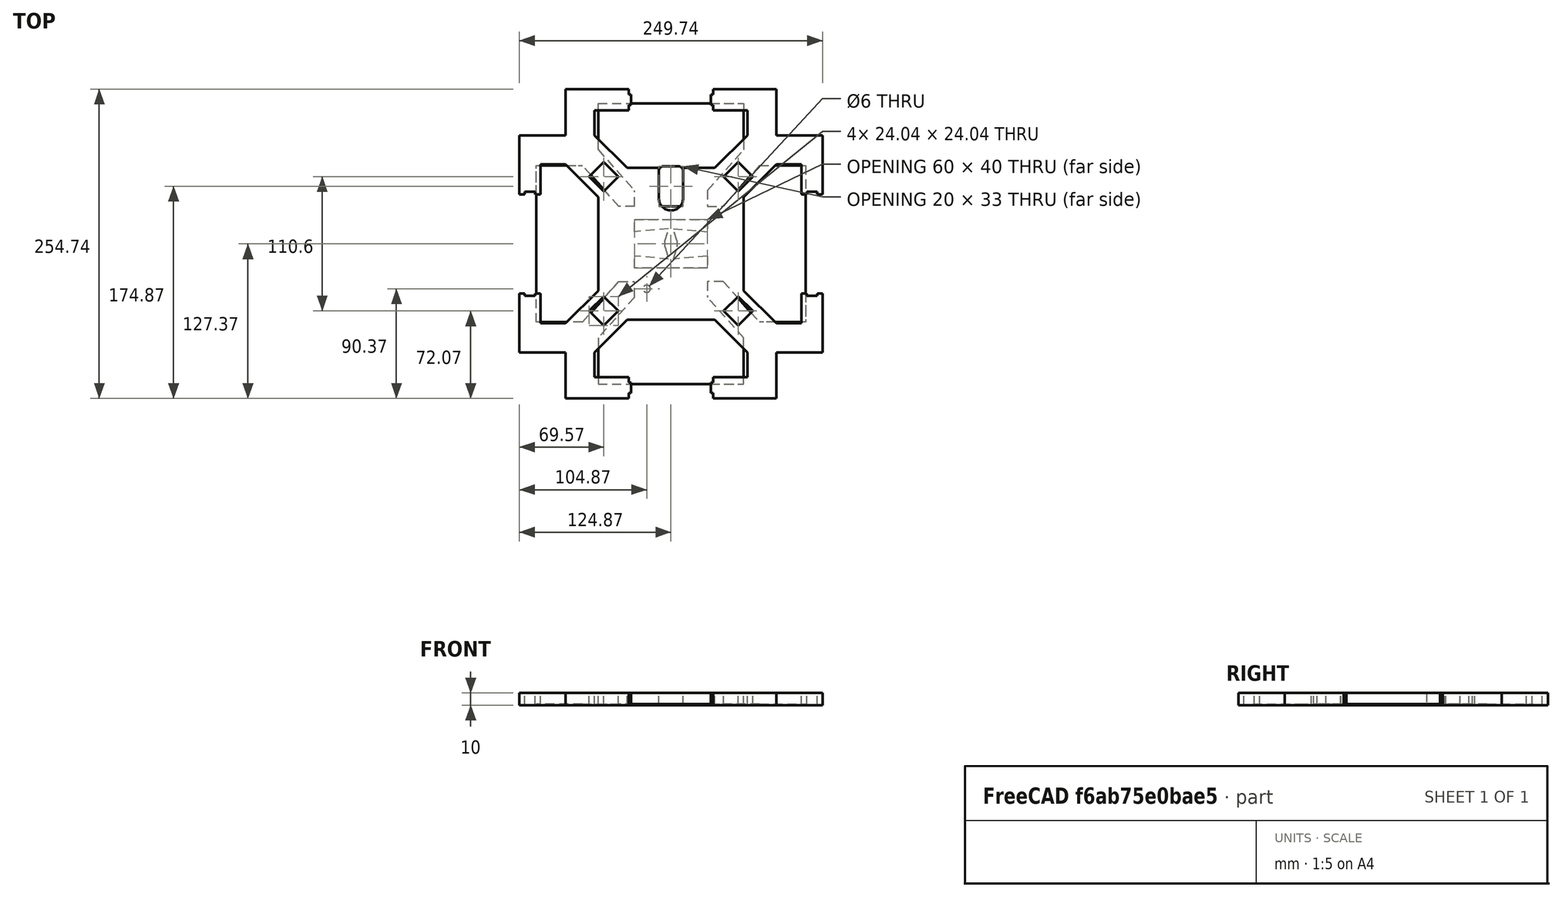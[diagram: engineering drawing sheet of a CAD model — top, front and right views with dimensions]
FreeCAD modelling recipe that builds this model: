
FCSTD DOCUMENT  (FreeCAD 0.20R29410 (Git))
Label: cardboard_insert
License: All rights reserved
LicenseURL: http://en.wikipedia.org/wiki/All_rights_reserved
objects: Sketcher::SketchObject×2, PartDesign::Pad×2, PartDesign::Body×2, TechDraw::DrawSVGTemplate×2, TechDraw::DrawProjGroupItem×2, TechDraw::DrawProjGroup×2, TechDraw::DrawViewDimension×2, TechDraw::DrawPage×2
note: 8 computed .brp shape members not serialized (recipe doc carries the construction recipe); baked Part::Feature solids carry a one-line shape summary decoded from their .brp

FEATURE [Sketcher::SketchObject] Sketch
  FullyConstrained = true
  MapMode = 5
  Support = -> [XY_Plane]
  expr: Constraints[378] = 6.65 + 1
  expr: Constraints[453] = 10.18 + 1
  sketch-geometry (214):
    g0: LineSegment StartX=53.3 StartY=53.3 StartZ=0 EndX=-53.3 EndY=53.3 EndZ=0
    g1: LineSegment StartX=-53.3 StartY=53.3 StartZ=0 EndX=-53.3 EndY=-53.3 EndZ=0
    g2: LineSegment StartX=-53.3 StartY=-53.3 StartZ=0 EndX=53.3 EndY=-53.3 EndZ=0
    g3: LineSegment StartX=53.3 StartY=-53.3 StartZ=0 EndX=53.3 EndY=53.3 EndZ=0
    g4: Circle CenterX=0 CenterY=0 CenterZ=0 NormalX=0 NormalY=0 NormalZ=1 AngleXU=0 Radius=75.3776
    g5: LineSegment StartX=-36.0792 StartY=62.5 StartZ=0 EndX=36.0792 EndY=62.5 EndZ=0
    g6: LineSegment StartX=-36.0792 StartY=-62.5 StartZ=0 EndX=36.0792 EndY=-62.5 EndZ=0
    g7: LineSegment StartX=-60 StartY=-38.5792 StartZ=0 EndX=-60 EndY=38.5792 EndZ=0
    g8: LineSegment StartX=60 StartY=38.5792 StartZ=0 EndX=60 EndY=-38.5792 EndZ=0
    g9: LineSegment StartX=36.0792 StartY=-62.5 StartZ=0 EndX=62.9492 EndY=-89.3701 EndZ=0
    g10: LineSegment StartX=60 StartY=-38.5792 StartZ=0 EndX=86.8701 EndY=-65.4492 EndZ=0
    g11: LineSegment StartX=60 StartY=38.5792 StartZ=0 EndX=86.8701 EndY=65.4492 EndZ=0
    g12: LineSegment StartX=36.0792 StartY=62.5 StartZ=0 EndX=62.9492 EndY=89.3701 EndZ=0
    g13: LineSegment StartX=62.9492 StartY=89.3701 StartZ=0 EndX=86.8701 EndY=65.4492 EndZ=0
    g14: LineSegment StartX=86.8701 StartY=-65.4492 StartZ=0 EndX=62.9492 EndY=-89.3701 EndZ=0
    g15: LineSegment StartX=-36.0792 StartY=-62.5 StartZ=0 EndX=-62.9492 EndY=-89.3701 EndZ=0
    g16: LineSegment StartX=-60 StartY=-38.5792 StartZ=0 EndX=-86.8701 EndY=-65.4492 EndZ=0
    g17: LineSegment StartX=-86.8701 StartY=-65.4492 StartZ=0 EndX=-62.9492 EndY=-89.3701 EndZ=0
    g18: LineSegment StartX=-60 StartY=38.5792 StartZ=0 EndX=-86.8701 EndY=65.4492 EndZ=0
    g19: LineSegment StartX=-86.8701 StartY=65.4492 StartZ=0 EndX=-62.9492 EndY=89.3701 EndZ=0
    g20: LineSegment StartX=-62.9492 StartY=89.3701 StartZ=0 EndX=-36.0792 EndY=62.5 EndZ=0
    g21: LineSegment StartX=-60 StartY=38.5792 StartZ=0 EndX=-7.1e-15 EndY=0 EndZ=0
    g22: LineSegment StartX=-7.1e-15 StartY=0 StartZ=0 EndX=60 EndY=-38.5792 EndZ=0
    g23: LineSegment StartX=60 StartY=38.5792 StartZ=0 EndX=0 EndY=0 EndZ=0
    g24: LineSegment StartX=0 StartY=0 StartZ=0 EndX=-60 EndY=-38.5792 EndZ=0
    g25: LineSegment StartX=0 StartY=0 StartZ=0 EndX=-36.0792 EndY=62.5 EndZ=0
    g26: LineSegment StartX=36.0792 StartY=62.5 StartZ=0 EndX=0 EndY=0 EndZ=0
    g27: LineSegment StartX=0 StartY=0 StartZ=0 EndX=-36.0792 EndY=-62.5 EndZ=0
    g28: LineSegment StartX=36.0792 StartY=-62.5 StartZ=0 EndX=0 EndY=0 EndZ=0
    g29: LineSegment StartX=-60 StartY=38.5792 StartZ=0 EndX=-36.0792 EndY=62.5 EndZ=0
    g30: LineSegment StartX=36.0792 StartY=62.5 StartZ=0 EndX=60 EndY=38.5792 EndZ=0
    g31: LineSegment StartX=60 StartY=-38.5792 StartZ=0 EndX=36.0792 EndY=-62.5 EndZ=0
    g32: LineSegment StartX=-36.0792 StartY=-62.5 StartZ=0 EndX=-60 EndY=-38.5792 EndZ=0
    g33: LineSegment StartX=-86.8701 StartY=65.4492 StartZ=0 EndX=-86.8701 EndY=89.3701 EndZ=0
    g34: LineSegment StartX=-86.8701 StartY=89.3701 StartZ=0 EndX=-62.9492 EndY=89.3701 EndZ=0
    g35: LineSegment StartX=62.9492 StartY=89.3701 StartZ=0 EndX=86.8701 EndY=89.3701 EndZ=0
    g36: LineSegment StartX=86.8701 StartY=89.3701 StartZ=0 EndX=86.8701 EndY=65.4492 EndZ=0
    g37: LineSegment StartX=62.9492 StartY=-89.3701 StartZ=0 EndX=86.8701 EndY=-89.3701 EndZ=0
    g38: LineSegment StartX=86.8701 StartY=-65.4492 StartZ=0 EndX=86.8701 EndY=-89.3701 EndZ=0
    g39: LineSegment StartX=-86.8701 StartY=-65.4492 StartZ=0 EndX=-86.8701 EndY=-89.3701 EndZ=0
    g40: LineSegment StartX=-62.9492 StartY=-89.3701 StartZ=0 EndX=-86.8701 EndY=-89.3701 EndZ=0
    g41: LineSegment StartX=-86.8701 StartY=65.4492 StartZ=0 EndX=-124.87 EndY=65.4492 EndZ=0
    g42: LineSegment StartX=-124.87 StartY=65.4492 StartZ=0 EndX=-124.87 EndY=89.3701 EndZ=0
    g43: LineSegment StartX=-124.87 StartY=89.3701 StartZ=0 EndX=-86.8701 EndY=89.3701 EndZ=0
    g44: LineSegment StartX=-86.8701 StartY=89.3701 StartZ=0 EndX=-86.8701 EndY=127.37 EndZ=0
    g45: LineSegment StartX=-86.8701 StartY=127.37 StartZ=0 EndX=-62.9492 EndY=127.37 EndZ=0
    g46: LineSegment StartX=-62.9492 StartY=127.37 StartZ=0 EndX=-62.9492 EndY=89.3701 EndZ=0
    g47: LineSegment StartX=-86.8701 StartY=-65.4492 StartZ=0 EndX=-124.87 EndY=-65.4492 EndZ=0
    g48: LineSegment StartX=-124.87 StartY=-65.4492 StartZ=0 EndX=-124.87 EndY=-89.3701 EndZ=0
    g49: LineSegment StartX=-124.87 StartY=-89.3701 StartZ=0 EndX=-86.8701 EndY=-89.3701 EndZ=0
    g50: LineSegment StartX=-86.8701 StartY=-89.3701 StartZ=0 EndX=-86.8701 EndY=-127.37 EndZ=0
    g51: LineSegment StartX=-86.8701 StartY=-127.37 StartZ=0 EndX=-62.9492 EndY=-127.37 EndZ=0
    g52: LineSegment StartX=-62.9492 StartY=-127.37 StartZ=0 EndX=-62.9492 EndY=-89.3701 EndZ=0
    g53: LineSegment StartX=62.9492 StartY=-89.3701 StartZ=0 EndX=62.9492 EndY=-127.37 EndZ=0
    g54: LineSegment StartX=62.9492 StartY=-127.37 StartZ=0 EndX=86.8701 EndY=-127.37 EndZ=0
    g55: LineSegment StartX=86.8701 StartY=-127.37 StartZ=0 EndX=86.8701 EndY=-89.3701 EndZ=0
    g56: LineSegment StartX=86.8701 StartY=-89.3701 StartZ=0 EndX=124.87 EndY=-89.3701 EndZ=0
    g57: LineSegment StartX=124.87 StartY=-89.3701 StartZ=0 EndX=124.87 EndY=-65.4492 EndZ=0
    g58: LineSegment StartX=124.87 StartY=-65.4492 StartZ=0 EndX=86.8701 EndY=-65.4492 EndZ=0
    g59: LineSegment StartX=86.8701 StartY=65.4492 StartZ=0 EndX=124.87 EndY=65.4492 EndZ=0
    g60: LineSegment StartX=124.87 StartY=65.4492 StartZ=0 EndX=124.87 EndY=89.3701 EndZ=0
    g61: LineSegment StartX=124.87 StartY=89.3701 StartZ=0 EndX=86.8701 EndY=89.3701 EndZ=0
    g62: LineSegment StartX=86.8701 StartY=89.3701 StartZ=0 EndX=86.8701 EndY=127.37 EndZ=0
    g63: LineSegment StartX=86.8701 StartY=127.37 StartZ=0 EndX=62.9492 EndY=127.37 EndZ=0
    g64: LineSegment StartX=62.9492 StartY=127.37 StartZ=0 EndX=62.9492 EndY=89.3701 EndZ=0
    g65: LineSegment StartX=-55.3 StartY=43.2792 StartZ=0 EndX=-67.3208 EndY=55.3 EndZ=0
    g66: LineSegment StartX=-67.3208 StartY=55.3 StartZ=0 EndX=-55.3 EndY=67.3208 EndZ=0
    g67: LineSegment StartX=-55.3 StartY=67.3208 StartZ=0 EndX=-43.2792 EndY=55.3 EndZ=0
    g68: LineSegment StartX=-43.2792 StartY=55.3 StartZ=0 EndX=-55.3 EndY=43.2792 EndZ=0
    g69: LineSegment StartX=43.2792 StartY=55.3 StartZ=0 EndX=55.3 EndY=67.3208 EndZ=0
    g70: LineSegment StartX=55.3 StartY=67.3208 StartZ=0 EndX=67.3208 EndY=55.3 EndZ=0
    g71: LineSegment StartX=67.3208 StartY=55.3 StartZ=0 EndX=55.3 EndY=43.2792 EndZ=0
    g72: LineSegment StartX=55.3 StartY=43.2792 StartZ=0 EndX=43.2792 EndY=55.3 EndZ=0
    g73: LineSegment StartX=43.2792 StartY=-55.3 StartZ=0 EndX=55.3 EndY=-67.3208 EndZ=0
    g74: LineSegment StartX=55.3 StartY=-67.3208 StartZ=0 EndX=67.3208 EndY=-55.3 EndZ=0
    g75: LineSegment StartX=67.3208 StartY=-55.3 StartZ=0 EndX=55.3 EndY=-43.2792 EndZ=0
    g76: LineSegment StartX=55.3 StartY=-43.2792 StartZ=0 EndX=43.2792 EndY=-55.3 EndZ=0
    g77: LineSegment StartX=-43.2792 StartY=-55.3 StartZ=0 EndX=-55.3 EndY=-67.3208 EndZ=0
    g78: LineSegment StartX=-55.3 StartY=-67.3208 StartZ=0 EndX=-67.3208 EndY=-55.3 EndZ=0
    g79: LineSegment StartX=-67.3208 StartY=-55.3 StartZ=0 EndX=-55.3 EndY=-43.2792 EndZ=0
    g80: LineSegment StartX=-55.3 StartY=-43.2792 StartZ=0 EndX=-43.2792 EndY=-55.3 EndZ=0
    g81: LineSegment StartX=-55.3 StartY=43.2792 StartZ=0 EndX=0 EndY=0 EndZ=0
    g82: LineSegment StartX=0 StartY=0 StartZ=0 EndX=-43.2792 EndY=55.3 EndZ=0
    g83: LineSegment StartX=43.2792 StartY=55.3 StartZ=0 EndX=0 EndY=0 EndZ=0
    g84: LineSegment StartX=0 StartY=0 StartZ=0 EndX=55.3 EndY=43.2792 EndZ=0
    g85: LineSegment StartX=55.3 StartY=-43.2792 StartZ=0 EndX=0 EndY=7.1e-15 EndZ=0
    g86: LineSegment StartX=0 StartY=0 StartZ=0 EndX=43.2792 EndY=-55.3 EndZ=0
    g87: LineSegment StartX=-43.2792 StartY=-55.3 StartZ=0 EndX=0 EndY=0 EndZ=0
    g88: LineSegment StartX=0 StartY=0 StartZ=0 EndX=-55.3 EndY=-43.2792 EndZ=0
    g89: LineSegment StartX=-124.87 StartY=65.4492 StartZ=0 EndX=-124.87 EndY=62.4492 EndZ=0
    g90: LineSegment StartX=-124.87 StartY=62.4492 StartZ=0 EndX=-107.37 EndY=62.4492 EndZ=0
    g91: LineSegment StartX=-107.37 StartY=62.4492 StartZ=0 EndX=-107.37 EndY=65.4492 EndZ=0
    g92: LineSegment StartX=-107.37 StartY=65.4492 StartZ=0 EndX=-86.8701 EndY=65.4492 EndZ=0
    g93: LineSegment StartX=-62.9492 StartY=89.3701 StartZ=0 EndX=-62.9492 EndY=109.87 EndZ=0
    g94: LineSegment StartX=-62.9492 StartY=109.87 StartZ=0 EndX=-59.9492 EndY=109.87 EndZ=0
    g95: LineSegment StartX=-59.9492 StartY=109.87 StartZ=0 EndX=-59.9492 EndY=127.37 EndZ=0
    g96: LineSegment StartX=-59.9492 StartY=127.37 StartZ=0 EndX=-62.9492 EndY=127.37 EndZ=0
    g97: LineSegment StartX=62.9492 StartY=127.37 StartZ=0 EndX=59.9492 EndY=127.37 EndZ=0
    g98: LineSegment StartX=59.9492 StartY=127.37 StartZ=0 EndX=59.9492 EndY=109.87 EndZ=0
    g99: LineSegment StartX=59.9492 StartY=109.87 StartZ=0 EndX=62.9492 EndY=109.87 EndZ=0
    g100: LineSegment StartX=62.9492 StartY=109.87 StartZ=0 EndX=62.9492 EndY=89.3701 EndZ=0
    g101: LineSegment StartX=86.8701 StartY=65.4492 StartZ=0 EndX=107.37 EndY=65.4492 EndZ=0
    g102: LineSegment StartX=107.37 StartY=65.4492 StartZ=0 EndX=107.37 EndY=62.4492 EndZ=0
    g103: LineSegment StartX=107.37 StartY=62.4492 StartZ=0 EndX=124.87 EndY=62.4492 EndZ=0
    g104: LineSegment StartX=124.87 StartY=62.4492 StartZ=0 EndX=124.87 EndY=65.4492 EndZ=0
    g105: LineSegment StartX=86.8701 StartY=-65.4492 StartZ=0 EndX=107.37 EndY=-65.4492 EndZ=0
    g106: LineSegment StartX=107.37 StartY=-65.4492 StartZ=0 EndX=107.37 EndY=-62.4492 EndZ=0
    g107: LineSegment StartX=107.37 StartY=-62.4492 StartZ=0 EndX=124.87 EndY=-62.4492 EndZ=0
    g108: LineSegment StartX=124.87 StartY=-62.4492 StartZ=0 EndX=124.87 EndY=-65.4492 EndZ=0
    g109: LineSegment StartX=62.9492 StartY=-89.3701 StartZ=0 EndX=62.9492 EndY=-109.87 EndZ=0
    g110: LineSegment StartX=62.9492 StartY=-109.87 StartZ=0 EndX=59.9492 EndY=-109.87 EndZ=0
    g111: LineSegment StartX=59.9492 StartY=-109.87 StartZ=0 EndX=59.9492 EndY=-127.37 EndZ=0
    g112: LineSegment StartX=59.9492 StartY=-127.37 StartZ=0 EndX=62.9492 EndY=-127.37 EndZ=0
    g113: LineSegment StartX=-62.9492 StartY=-127.37 StartZ=0 EndX=-59.9492 EndY=-127.37 EndZ=0
    g114: LineSegment StartX=-59.9492 StartY=-127.37 StartZ=0 EndX=-59.9492 EndY=-109.87 EndZ=0
    g115: LineSegment StartX=-59.9492 StartY=-109.87 StartZ=0 EndX=-62.9492 EndY=-109.87 EndZ=0
    g116: LineSegment StartX=-62.9492 StartY=-109.87 StartZ=0 EndX=-62.9492 EndY=-89.3701 EndZ=0
    g117: LineSegment StartX=-124.87 StartY=-65.4492 StartZ=0 EndX=-124.87 EndY=-62.4492 EndZ=0
    g118: LineSegment StartX=-124.87 StartY=-62.4492 StartZ=0 EndX=-107.37 EndY=-62.4492 EndZ=0
    g119: LineSegment StartX=-107.37 StartY=-62.4492 StartZ=0 EndX=-107.37 EndY=-65.4492 EndZ=0
    g120: LineSegment StartX=-107.37 StartY=-65.4492 StartZ=0 EndX=-86.8701 EndY=-65.4492 EndZ=0
    g121: LineSegment StartX=-124.87 StartY=62.4492 StartZ=0 EndX=-124.87 EndY=54.7992 EndZ=0
    g122: LineSegment StartX=-124.87 StartY=54.7992 StartZ=0 EndX=-107.37 EndY=54.7992 EndZ=0
    g123: LineSegment StartX=-107.37 StartY=54.7992 StartZ=0 EndX=-107.37 EndY=62.4492 EndZ=0
    g124: LineSegment StartX=-59.9492 StartY=127.37 StartZ=0 EndX=-48.7692 EndY=127.37 EndZ=0
    g125: LineSegment StartX=-48.7692 StartY=127.37 StartZ=0 EndX=-48.7692 EndY=109.87 EndZ=0
    g126: LineSegment StartX=-48.7692 StartY=109.87 StartZ=0 EndX=-59.9492 EndY=109.87 EndZ=0
    g127: LineSegment StartX=59.9492 StartY=127.37 StartZ=0 EndX=48.7692 EndY=127.37 EndZ=0
    g128: LineSegment StartX=48.7692 StartY=127.37 StartZ=0 EndX=48.7692 EndY=109.87 EndZ=0
    g129: LineSegment StartX=48.7692 StartY=109.87 StartZ=0 EndX=59.9492 EndY=109.87 EndZ=0
    g130: LineSegment StartX=107.37 StartY=62.4492 StartZ=0 EndX=107.37 EndY=54.7992 EndZ=0
    g131: LineSegment StartX=107.37 StartY=54.7992 StartZ=0 EndX=124.87 EndY=54.7992 EndZ=0
    g132: LineSegment StartX=124.87 StartY=54.7992 StartZ=0 EndX=124.87 EndY=62.4492 EndZ=0
    g133: LineSegment StartX=107.37 StartY=-62.4492 StartZ=0 EndX=107.37 EndY=-54.7992 EndZ=0
    g134: LineSegment StartX=107.37 StartY=-54.7992 StartZ=0 EndX=124.87 EndY=-54.7992 EndZ=0
    g135: LineSegment StartX=124.87 StartY=-54.7992 StartZ=0 EndX=124.87 EndY=-62.4492 EndZ=0
    g136: LineSegment StartX=59.9492 StartY=-109.87 StartZ=0 EndX=48.7692 EndY=-109.87 EndZ=0
    g137: LineSegment StartX=48.7692 StartY=-109.87 StartZ=0 EndX=48.7692 EndY=-127.37 EndZ=0
    g138: LineSegment StartX=48.7692 StartY=-127.37 StartZ=0 EndX=59.9492 EndY=-127.37 EndZ=0
    g139: LineSegment StartX=-59.9492 StartY=-127.37 StartZ=0 EndX=-48.7692 EndY=-127.37 EndZ=0
    g140: LineSegment StartX=-48.7692 StartY=-127.37 StartZ=0 EndX=-48.7692 EndY=-109.87 EndZ=0
    g141: LineSegment StartX=-48.7692 StartY=-109.87 StartZ=0 EndX=-59.9492 EndY=-109.87 EndZ=0
    g142: LineSegment StartX=-124.87 StartY=-62.4492 StartZ=0 EndX=-124.87 EndY=-54.7992 EndZ=0
    g143: LineSegment StartX=-124.87 StartY=-54.7992 StartZ=0 EndX=-107.37 EndY=-54.7992 EndZ=0
    g144: LineSegment StartX=-107.37 StartY=-54.7992 StartZ=0 EndX=-107.37 EndY=-62.4492 EndZ=0
    g145: LineSegment StartX=-36.0792 StartY=62.5 StartZ=0 EndX=-10 EndY=62.5 EndZ=0
    g146: LineSegment StartX=36.0792 StartY=62.5 StartZ=0 EndX=10 EndY=62.5 EndZ=0
    g147: LineSegment StartX=-10 StartY=62.5 StartZ=0 EndX=-10 EndY=37.5 EndZ=0
    g148: LineSegment StartX=10 StartY=62.5 StartZ=0 EndX=10 EndY=37.5 EndZ=0
    g149: ArcOfCircle CenterX=0 CenterY=37.5 CenterZ=0 NormalX=0 NormalY=0 NormalZ=1 AngleXU=0 Radius=10 StartAngle=3.14159 EndAngle=6.28319
    g150: LineSegment StartX=-124.87 StartY=54.7992 StartZ=0 EndX=-124.87 EndY=40.7992 EndZ=0
    g151: LineSegment StartX=-124.87 StartY=40.7992 StartZ=0 EndX=-107.37 EndY=40.7992 EndZ=0
    g152: LineSegment StartX=-107.37 StartY=40.7992 StartZ=0 EndX=-107.37 EndY=54.7992 EndZ=0
    g153: LineSegment StartX=-48.7692 StartY=127.37 StartZ=0 EndX=-34.7692 EndY=127.37 EndZ=0
    g154: LineSegment StartX=-34.7692 StartY=127.37 StartZ=0 EndX=-34.7692 EndY=109.87 EndZ=0
    g155: LineSegment StartX=-34.7692 StartY=109.87 StartZ=0 EndX=-48.7692 EndY=109.87 EndZ=0
    g156: LineSegment StartX=48.7692 StartY=127.37 StartZ=0 EndX=34.7692 EndY=127.37 EndZ=0
    g157: LineSegment StartX=34.7692 StartY=127.37 StartZ=0 EndX=34.7692 EndY=109.87 EndZ=0
    g158: LineSegment StartX=34.7692 StartY=109.87 StartZ=0 EndX=48.7692 EndY=109.87 EndZ=0
    g159: LineSegment StartX=107.37 StartY=54.7992 StartZ=0 EndX=107.37 EndY=40.7992 EndZ=0
    g160: LineSegment StartX=107.37 StartY=40.7992 StartZ=0 EndX=124.87 EndY=40.7992 EndZ=0
    g161: LineSegment StartX=124.87 StartY=40.7992 StartZ=0 EndX=124.87 EndY=54.7992 EndZ=0
    g162: LineSegment StartX=124.87 StartY=-54.7992 StartZ=0 EndX=124.87 EndY=-40.7992 EndZ=0
    g163: LineSegment StartX=124.87 StartY=-40.7992 StartZ=0 EndX=107.37 EndY=-40.7992 EndZ=0
    g164: LineSegment StartX=107.37 StartY=-40.7992 StartZ=0 EndX=107.37 EndY=-54.7992 EndZ=0
    g165: LineSegment StartX=48.7692 StartY=-109.87 StartZ=0 EndX=34.7692 EndY=-109.87 EndZ=0
    g166: LineSegment StartX=34.7692 StartY=-109.87 StartZ=0 EndX=34.7692 EndY=-127.37 EndZ=0
    g167: LineSegment StartX=34.7692 StartY=-127.37 StartZ=0 EndX=48.7692 EndY=-127.37 EndZ=0
    g168: LineSegment StartX=-48.7692 StartY=-109.87 StartZ=0 EndX=-34.7692 EndY=-109.87 EndZ=0
    g169: LineSegment StartX=-34.7692 StartY=-109.87 StartZ=0 EndX=-34.7692 EndY=-127.37 EndZ=0
    g170: LineSegment StartX=-34.7692 StartY=-127.37 StartZ=0 EndX=-48.7692 EndY=-127.37 EndZ=0
    g171: LineSegment StartX=-124.87 StartY=-54.7992 StartZ=0 EndX=-124.87 EndY=-40.7992 EndZ=0
    g172: LineSegment StartX=-124.87 StartY=-40.7992 StartZ=0 EndX=-107.37 EndY=-40.7992 EndZ=0
    g173: LineSegment StartX=-107.37 StartY=-40.7992 StartZ=0 EndX=-107.37 EndY=-54.7992 EndZ=0
    g174: LineSegment StartX=-124.87 StartY=40.7992 StartZ=0 EndX=-120.37 EndY=40.7992 EndZ=0
    g175: LineSegment StartX=-120.37 StartY=40.7992 StartZ=0 EndX=-120.37 EndY=42.7992 EndZ=0
    g176: LineSegment StartX=-120.37 StartY=42.7992 StartZ=0 EndX=-111.87 EndY=42.7992 EndZ=0
    g177: LineSegment StartX=-111.87 StartY=42.7992 StartZ=0 EndX=-111.87 EndY=40.7992 EndZ=0
    g178: LineSegment StartX=-111.87 StartY=40.7992 StartZ=0 EndX=-107.37 EndY=40.7992 EndZ=0
    g179: LineSegment StartX=107.37 StartY=40.7992 StartZ=0 EndX=111.87 EndY=40.7992 EndZ=0
    g180: LineSegment StartX=111.87 StartY=40.7992 StartZ=0 EndX=111.87 EndY=42.7992 EndZ=0
    g181: LineSegment StartX=111.87 StartY=42.7992 StartZ=0 EndX=120.37 EndY=42.7992 EndZ=0
    g182: LineSegment StartX=120.37 StartY=42.7992 StartZ=0 EndX=120.37 EndY=40.7992 EndZ=0
    g183: LineSegment StartX=120.37 StartY=40.7992 StartZ=0 EndX=124.87 EndY=40.7992 EndZ=0
    g184: LineSegment StartX=107.37 StartY=-40.7992 StartZ=0 EndX=111.87 EndY=-40.7992 EndZ=0
    g185: LineSegment StartX=111.87 StartY=-40.7992 StartZ=0 EndX=111.87 EndY=-42.7992 EndZ=0
    g186: LineSegment StartX=111.87 StartY=-42.7992 StartZ=0 EndX=120.37 EndY=-42.7992 EndZ=0
    g187: LineSegment StartX=120.37 StartY=-42.7992 StartZ=0 EndX=120.37 EndY=-40.7992 EndZ=0
    g188: LineSegment StartX=120.37 StartY=-40.7992 StartZ=0 EndX=124.87 EndY=-40.7992 EndZ=0
    g189: LineSegment StartX=-124.87 StartY=-40.7992 StartZ=0 EndX=-120.37 EndY=-40.7992 EndZ=0
    g190: LineSegment StartX=-120.37 StartY=-40.7992 StartZ=0 EndX=-120.37 EndY=-42.7992 EndZ=0
    g191: LineSegment StartX=-120.37 StartY=-42.7992 StartZ=0 EndX=-111.87 EndY=-42.7992 EndZ=0
    g192: LineSegment StartX=-111.87 StartY=-42.7992 StartZ=0 EndX=-111.87 EndY=-40.7992 EndZ=0
    g193: LineSegment StartX=-111.87 StartY=-40.7992 StartZ=0 EndX=-107.37 EndY=-40.7992 EndZ=0
    g194: LineSegment StartX=-34.7692 StartY=127.37 StartZ=0 EndX=-34.7692 EndY=122.87 EndZ=0
    g195: LineSegment StartX=-34.7692 StartY=122.87 StartZ=0 EndX=-32.7692 EndY=122.87 EndZ=0
    g196: LineSegment StartX=-32.7692 StartY=122.87 StartZ=0 EndX=-32.7692 EndY=114.37 EndZ=0
    g197: LineSegment StartX=-32.7692 StartY=114.37 StartZ=0 EndX=-34.7692 EndY=114.37 EndZ=0
    g198: LineSegment StartX=-34.7692 StartY=114.37 StartZ=0 EndX=-34.7692 EndY=109.87 EndZ=0
    g199: LineSegment StartX=34.7692 StartY=127.37 StartZ=0 EndX=34.7692 EndY=122.87 EndZ=0
    g200: LineSegment StartX=34.7692 StartY=122.87 StartZ=0 EndX=32.7692 EndY=122.87 EndZ=0
    g201: LineSegment StartX=32.7692 StartY=122.87 StartZ=0 EndX=32.7692 EndY=114.37 EndZ=0
    g202: LineSegment StartX=32.7692 StartY=114.37 StartZ=0 EndX=34.7692 EndY=114.37 EndZ=0
    g203: LineSegment StartX=34.7692 StartY=114.37 StartZ=0 EndX=34.7692 EndY=109.87 EndZ=0
    g204: LineSegment StartX=-34.7692 StartY=-109.87 StartZ=0 EndX=-34.7692 EndY=-114.37 EndZ=0
    g205: LineSegment StartX=-34.7692 StartY=-114.37 StartZ=0 EndX=-32.7692 EndY=-114.37 EndZ=0
    g206: LineSegment StartX=-32.7692 StartY=-114.37 StartZ=0 EndX=-32.7692 EndY=-122.87 EndZ=0
    g207: LineSegment StartX=-32.7692 StartY=-122.87 StartZ=0 EndX=-34.7692 EndY=-122.87 EndZ=0
    g208: LineSegment StartX=-34.7692 StartY=-122.87 StartZ=0 EndX=-34.7692 EndY=-127.37 EndZ=0
    g209: LineSegment StartX=34.7692 StartY=-109.87 StartZ=0 EndX=34.7692 EndY=-114.37 EndZ=0
    g210: LineSegment StartX=34.7692 StartY=-114.37 StartZ=0 EndX=32.7692 EndY=-114.37 EndZ=0
    g211: LineSegment StartX=32.7692 StartY=-114.37 StartZ=0 EndX=32.7692 EndY=-122.87 EndZ=0
    g212: LineSegment StartX=32.7692 StartY=-122.87 StartZ=0 EndX=34.7692 EndY=-122.87 EndZ=0
    g213: LineSegment StartX=34.7692 StartY=-122.87 StartZ=0 EndX=34.7692 EndY=-127.37 EndZ=0
  constraints (575):
    c: Coincident(g0,g1)
    c: Coincident(g1,g2)
    c: Coincident(g2,g3)
    c: Coincident(g3,g0)
    c: Equal(g0,g1)
    c: Equal(g0,g2)
    c: Equal(g0,g3)
    c: PointOnObject(g0,g4)
    c: PointOnObject(g1,g4)
    c: PointOnObject(g2,g4)
    c: PointOnObject(g3,g4)
    c: Coincident(g4,g-1)
    c: Horizontal(g0)
    c: DistanceX(g0,g0) = 106.6
    c: Horizontal(g5)
    c: Horizontal(g6)
    c: Vertical(g7)
    c: Vertical(g8)
    c: Coincident(g9,g6)
    c: Coincident(g10,g8)
    c: Coincident(g11,g8)
    c: Coincident(g12,g5)
    c: Coincident(g13,g12)
    c: Coincident(g13,g11)
    c: Coincident(g14,g10)
    c: Coincident(g14,g9)
    c: Coincident(g15,g6)
    c: Coincident(g7,g16)
    c: Coincident(g16,g17)
    c: Coincident(g17,g15)
    c: Coincident(g7,g18)
    c: Coincident(g18,g19)
    c: Coincident(g19,g20)
    c: Coincident(g20,g5)
    c: Perpendicular(g19,g18)
    c: Perpendicular(g20,g19)
    c: Perpendicular(g13,g12)
    c: Perpendicular(g11,g13)
    c: Perpendicular(g14,g10)
    c: Perpendicular(g9,g14)
    c: Perpendicular(g17,g15)
    c: Perpendicular(g16,g17)
    c: Parallel(g16,g19)
    c: Parallel(g19,g12)
    c: Parallel(g12,g14)
    c: Angle(g5,g20) = 2.35619
    c: Coincident(g7,g21)
    c: Coincident(g21,g-1)
    c: Coincident(g21,g22)
    c: Coincident(g22,g8)
    c: Coincident(g8,g23)
    c: Coincident(g23,g-1)
    c: Coincident(g23,g24)
    c: Coincident(g24,g7)
    c: Coincident(g-1,g25)
    c: Coincident(g25,g5)
    c: Coincident(g5,g26)
    c: Coincident(g26,g-1)
    c: Coincident(g26,g27)
    c: Coincident(g27,g6)
    c: Coincident(g6,g28)
    c: Coincident(g28,g-1)
    c: Equal(g27,g28)
    c: Equal(g28,g26)
    c: Equal(g26,g25)
    c: Equal(g21,g24)
    c: Equal(g24,g22)
    c: Equal(g22,g23)
    c: DistanceX(g7,g8) = 120
    c: DistanceY(g6,g5) = 125
    c: Coincident(g29,g7)
    c: Coincident(g29,g5)
    c: Coincident(g30,g5)
    c: Coincident(g30,g8)
    c: Coincident(g31,g8)
    c: Coincident(g31,g6)
    c: Coincident(g32,g6)
    c: Coincident(g32,g7)
    c: Parallel(g32,g17)
    c: Parallel(g29,g19)
    c: Parallel(g30,g13)
    c: Equal(g20,g12)
    c: Equal(g12,g15)
    c: Equal(g15,g9)
    c: Coincident(g18,g33)
    c: Vertical(g33)
    c: Coincident(g33,g34)
    c: Coincident(g34,g19)
    c: Horizontal(g34)
    c: Coincident(g35,g12)
    c: Horizontal(g35)
    c: Coincident(g36,g35)
    c: Coincident(g36,g11)
    c: Vertical(g36)
    c: Coincident(g37,g9)
    c: Horizontal(g37)
    c: Coincident(g38,g10)
    c: Coincident(g38,g37)
    c: Vertical(g38)
    c: Coincident(g39,g16)
    c: Vertical(g39)
    c: Coincident(g40,g15)
    c: Coincident(g40,g39)
    c: Horizontal(g40)
    c: Distance(g20) = 38
    c: Coincident(g18,g41)
    c: Horizontal(g41)
    c: Coincident(g41,g42)
    c: Vertical(g42)
    c: Coincident(g42,g43)
    c: Coincident(g43,g33)
    c: Horizontal(g43)
    c: Coincident(g43,g44)
    c: Vertical(g44)
    c: Coincident(g44,g45)
    c: Horizontal(g45)
    c: Coincident(g45,g46)
    c: Coincident(g46,g20)
    c: Vertical(g46)
    c: Coincident(g16,g47)
    c: Horizontal(g47)
    c: Coincident(g47,g48)
    c: Vertical(g48)
    c: Coincident(g48,g49)
    c: Coincident(g49,g39)
    c: Coincident(g49,g50)
    c: Vertical(g50)
    c: Coincident(g50,g51)
    c: Horizontal(g51)
    c: Coincident(g51,g52)
    c: Coincident(g52,g15)
    c: Vertical(g52)
    c: Horizontal(g49)
    c: Coincident(g9,g53)
    c: Vertical(g53)
    c: Coincident(g53,g54)
    c: Horizontal(g54)
    c: Coincident(g54,g55)
    c: Coincident(g55,g37)
    c: Vertical(g55)
    c: Coincident(g55,g56)
    c: Horizontal(g56)
    c: Coincident(g56,g57)
    c: Vertical(g57)
    c: Coincident(g57,g58)
    c: Coincident(g58,g10)
    c: Horizontal(g58)
    c: Coincident(g11,g59)
    c: Horizontal(g59)
    c: Coincident(g59,g60)
    c: Vertical(g60)
    c: Coincident(g60,g61)
    c: Coincident(g61,g35)
    c: Horizontal(g61)
    c: Coincident(g61,g62)
    c: Vertical(g62)
    c: Coincident(g62,g63)
    c: Horizontal(g63)
    c: Coincident(g63,g64)
    c: Coincident(g64,g12)
    c: Vertical(g64)
    c: Equal(g44,g43)
    c: Equal(g43,g20)
    c: Equal(g61,g62)
    c: Equal(g62,g12)
    c: Equal(g56,g55)
    c: Equal(g55,g9)
    c: Equal(g49,g50)
    c: Equal(g50,g15)
    c: PointOnObject(g65,g29)
    c: Coincident(g65,g66)
    c: Coincident(g66,g67)
    c: PointOnObject(g67,g29)
    c: Coincident(g67,g68)
    c: Coincident(g68,g65)
    c: PointOnObject(g69,g30)
    c: Coincident(g69,g70)
    c: Coincident(g70,g71)
    c: PointOnObject(g71,g30)
    c: Coincident(g71,g72)
    c: Coincident(g72,g69)
    c: PointOnObject(g73,g31)
    c: Coincident(g73,g74)
    c: Coincident(g74,g75)
    c: PointOnObject(g75,g31)
    c: Coincident(g75,g76)
    c: Coincident(g76,g73)
    c: PointOnObject(g77,g32)
    c: Coincident(g77,g78)
    c: Coincident(g78,g79)
    c: PointOnObject(g79,g32)
    c: Coincident(g79,g80)
    c: Coincident(g80,g77)
    c: Parallel(g78,g80)
    c: Parallel(g68,g66)
    c: Parallel(g72,g70)
    c: Parallel(g76,g74)
    c: Coincident(g65,g81)
    c: Coincident(g81,g-1)
    c: Coincident(g81,g82)
    c: Coincident(g82,g67)
    c: Coincident(g69,g83)
    c: Coincident(g83,g-1)
    c: Coincident(g83,g84)
    c: Coincident(g84,g71)
    c: Coincident(g75,g85)
    c: Coincident(g85,g-1)
    c: Coincident(g85,g86)
    c: Coincident(g86,g73)
    c: Coincident(g77,g87)
    c: Coincident(g87,g-1)
    c: Coincident(g87,g88)
    c: Coincident(g88,g79)
    c: Equal(g87,g88)
    c: Equal(g88,g81)
    c: Equal(g81,g82)
    c: Equal(g82,g83)
    c: Equal(g83,g84)
    c: Equal(g84,g85)
    c: Equal(g85,g86)
    c: Parallel(g67,g65)
    c: Parallel(g65,g20)
    c: Parallel(g71,g69)
    c: Parallel(g69,g12)
    c: Parallel(g79,g77)
    c: Parallel(g77,g15)
    c: Parallel(g9,g73)
    c: Parallel(g73,g75)
    c: Distance(g67) = 17
    c: Coincident(g42,g89)
    c: Vertical(g89)
    c: Coincident(g89,g90)
    c: Horizontal(g90)
    c: Coincident(g90,g91)
    c: Coincident(g91,g92)
    c: Vertical(g91)
    c: Coincident(g93,g94)
    c: Horizontal(g94)
    c: Coincident(g94,g95)
    c: Vertical(g95)
    c: Coincident(g95,g96)
    c: Coincident(g96,g45)
    c: Horizontal(g96)
    c: Coincident(g63,g97)
    c: Horizontal(g97)
    c: Coincident(g97,g98)
    c: Vertical(g98)
    c: Coincident(g98,g99)
    c: Horizontal(g99)
    c: Coincident(g99,g100)
    c: Coincident(g101,g102)
    c: Vertical(g102)
    c: Coincident(g102,g103)
    c: Horizontal(g103)
    c: Coincident(g103,g104)
    c: Coincident(g104,g60)
    c: Vertical(g104)
    c: Coincident(g105,g106)
    c: Vertical(g106)
    c: Coincident(g106,g107)
    c: Horizontal(g107)
    c: Coincident(g107,g108)
    c: Coincident(g108,g57)
    c: Vertical(g108)
    c: Coincident(g109,g110)
    c: Horizontal(g110)
    c: Coincident(g110,g111)
    c: Vertical(g111)
    c: Coincident(g111,g112)
    c: Coincident(g112,g54)
    c: Horizontal(g112)
    c: Coincident(g51,g113)
    c: Horizontal(g113)
    c: Coincident(g113,g114)
    c: Vertical(g114)
    c: Coincident(g114,g115)
    c: Horizontal(g115)
    c: Coincident(g115,g116)
    c: Coincident(g48,g117)
    c: Vertical(g117)
    c: Coincident(g117,g118)
    c: Horizontal(g118)
    c: Coincident(g118,g119)
    c: Vertical(g119)
    c: Coincident(g119,g120)
    c: Equal(g92,g120)
    c: Equal(g120,g116)
    c: Equal(g116,g109)
    c: Equal(g109,g105)
    c: Equal(g105,g101)
    c: Equal(g101,g100)
    c: Equal(g100,g93)
    c: Equal(g94,g91)
    c: Equal(g91,g99)
    c: Equal(g99,g102)
    c: Equal(g102,g106)
    c: Equal(g106,g110)
    c: Equal(g110,g115)
    c: Equal(g115,g119)
    c: Distance(g66) = 17
    c: DistanceY(g0,g67) = 2
    c: Equal(g89,g96)
    c: DistanceX(g90,g90) = 17.5
    c: Coincident(g120,g16)
    c: Coincident(g92,g18)
    c: Coincident(g93,g20)
    c: Coincident(g100,g12)
    c: Coincident(g101,g11)
    c: Coincident(g105,g10)
    c: Coincident(g109,g9)
    c: Coincident(g116,g15)
    c: Horizontal(g120)
    c: Vertical(g116)
    c: Vertical(g109)
    c: Horizontal(g105)
    c: Horizontal(g101)
    c: Vertical(g100)
    c: Vertical(g93)
    c: Equal(g69,g67)
    c: Equal(g79,g67)
    c: Equal(g75,g67)
    c: DistanceY(g89,g89) = 3
    c: Coincident(g89,g121)
    c: Vertical(g121)
    c: Coincident(g121,g122)
    c: Horizontal(g122)
    c: Coincident(g122,g123)
    c: Coincident(g123,g91)
    c: Vertical(g123)
    c: Coincident(g96,g124)
    c: Horizontal(g124)
    c: Coincident(g124,g125)
    c: Vertical(g125)
    c: Coincident(g125,g126)
    c: Coincident(g126,g94)
    c: Horizontal(g126)
    c: Coincident(g97,g127)
    c: Horizontal(g127)
    c: Coincident(g127,g128)
    c: Vertical(g128)
    c: Coincident(g128,g129)
    c: Coincident(g129,g99)
    c: Horizontal(g129)
    c: Coincident(g102,g130)
    c: Vertical(g130)
    c: Coincident(g130,g131)
    c: Horizontal(g131)
    c: Coincident(g131,g132)
    c: Coincident(g132,g104)
    c: Vertical(g132)
    c: Coincident(g106,g133)
    c: Vertical(g133)
    c: Coincident(g133,g134)
    c: Horizontal(g134)
    c: Coincident(g134,g135)
    c: Coincident(g135,g108)
    c: Vertical(g135)
    c: Coincident(g110,g136)
    c: Horizontal(g136)
    c: Coincident(g136,g137)
    c: Vertical(g137)
    c: Coincident(g137,g138)
    c: Coincident(g138,g112)
    c: Horizontal(g138)
    c: Coincident(g113,g139)
    c: Horizontal(g139)
    c: Coincident(g139,g140)
    c: Vertical(g140)
    c: Coincident(g140,g141)
    c: Coincident(g141,g115)
    c: Horizontal(g141)
    c: Coincident(g117,g142)
    c: Vertical(g142)
    c: Coincident(g142,g143)
    c: Horizontal(g143)
    c: Coincident(g143,g144)
    c: Coincident(g144,g119)
    c: Vertical(g144)
    c: DistanceY(g121,g121) = 7.65
    c: Coincident(g145,g20)
    c: PointOnObject(g145,g5)
    c: Coincident(g12,g146)
    c: PointOnObject(g146,g5)
    c: Coincident(g145,g147)
    c: Vertical(g147)
    c: Coincident(g146,g148)
    c: Vertical(g148)
    c: PointOnObject(g149,g-2)
    c: Tangent(g149,g147) = -1.5708
    c: Tangent(g149,g148) = 1.5708
    c: DistanceY(g147,g147) = 25
    c: Radius(g149) = 10
    c: Coincident(g121,g150)
    c: Vertical(g150)
    c: Coincident(g150,g151)
    c: Horizontal(g151)
    c: Coincident(g151,g152)
    c: Coincident(g152,g123)
    c: Vertical(g152)
    c: Coincident(g124,g153)
    c: Horizontal(g153)
    c: Coincident(g153,g154)
    c: Vertical(g154)
    c: Coincident(g154,g155)
    c: Coincident(g155,g126)
    c: Horizontal(g155)
    c: Coincident(g127,g156)
    c: Horizontal(g156)
    c: Coincident(g156,g157)
    c: Vertical(g157)
    c: Coincident(g157,g158)
    c: Coincident(g158,g129)
    c: Horizontal(g158)
    c: Coincident(g130,g159)
    c: Vertical(g159)
    c: Coincident(g159,g160)
    c: Coincident(g160,g161)
    c: Coincident(g161,g132)
    c: Vertical(g161)
    c: Horizontal(g160)
    c: Coincident(g135,g162)
    c: Vertical(g162)
    c: Coincident(g162,g163)
    c: Horizontal(g163)
    c: Coincident(g163,g164)
    c: Coincident(g164,g133)
    c: Vertical(g164)
    c: Coincident(g136,g165)
    c: Horizontal(g165)
    c: Coincident(g165,g166)
    c: Vertical(g166)
    c: Coincident(g166,g167)
    c: Coincident(g167,g138)
    c: Horizontal(g167)
    c: Coincident(g141,g168)
    c: Horizontal(g168)
    c: Coincident(g168,g169)
    c: Vertical(g169)
    c: Coincident(g169,g170)
    c: Coincident(g170,g139)
    c: Horizontal(g170)
    c: Coincident(g142,g171)
    c: Vertical(g171)
    c: Coincident(g171,g172)
    c: Horizontal(g172)
    c: Coincident(g172,g173)
    c: Vertical(g173)
    c: Equal(g121,g132)
    c: Equal(g132,g135)
    c: Equal(g135,g142)
    c: Equal(g124,g127)
    c: Equal(g127,g139)
    c: Equal(g139,g138)
    c: DistanceX(g124,g124) = 11.18
    c: Equal(g150,g153)
    c: Equal(g153,g156)
    c: Equal(g156,g161)
    c: Equal(g161,g162)
    c: Equal(g162,g167)
    c: Equal(g167,g170)
    c: Equal(g170,g171)
    c: DistanceY(g150,g150) = 14
    c: Coincident(g173,g144)
    c: Coincident(g150,g174)
    c: Horizontal(g174)
    c: Coincident(g174,g175)
    c: Vertical(g175)
    c: Coincident(g175,g176)
    c: Coincident(g176,g177)
    c: Coincident(g177,g178)
    c: Coincident(g178,g152)
    c: Horizontal(g178)
    c: Vertical(g177)
    c: Horizontal(g176)
    c: Coincident(g159,g179)
    c: Coincident(g179,g180)
    c: Vertical(g180)
    c: Coincident(g180,g181)
    c: Horizontal(g181)
    c: Coincident(g182,g181)
    c: Vertical(g182)
    c: Coincident(g183,g182)
    c: Coincident(g183,g161)
    c: Horizontal(g183)
    c: Horizontal(g179)
    c: Coincident(g164,g184)
    c: Coincident(g184,g185)
    c: Vertical(g185)
    c: Coincident(g185,g186)
    c: Horizontal(g186)
    c: Coincident(g186,g187)
    c: Vertical(g187)
    c: Coincident(g187,g188)
    c: Coincident(g188,g162)
    c: Horizontal(g188)
    c: Horizontal(g184)
    c: Coincident(g171,g189)
    c: Coincident(g189,g190)
    c: Vertical(g190)
    c: Coincident(g190,g191)
    c: Coincident(g191,g192)
    c: Vertical(g192)
    c: Coincident(g192,g193)
    c: Coincident(g193,g173)
    c: Horizontal(g191)
    c: Horizontal(g193)
    c: Horizontal(g189)
    c: Coincident(g153,g194)
    c: Coincident(g194,g195)
    c: Horizontal(g195)
    c: Coincident(g195,g196)
    c: Vertical(g196)
    c: Coincident(g196,g197)
    c: Horizontal(g197)
    c: Coincident(g197,g198)
    c: Coincident(g198,g155)
    c: Coincident(g156,g199)
    c: Coincident(g199,g200)
    c: Horizontal(g200)
    c: Coincident(g200,g201)
    c: Vertical(g201)
    c: Coincident(g201,g202)
    c: Horizontal(g202)
    c: Coincident(g202,g203)
    c: Coincident(g203,g158)
    c: Vertical(g194)
    c: Vertical(g198)
    c: Vertical(g203)
    c: Vertical(g199)
    c: Coincident(g168,g204)
    c: Coincident(g204,g205)
    c: Coincident(g205,g206)
    c: Vertical(g206)
    c: Coincident(g206,g207)
    c: Coincident(g207,g208)
    c: Coincident(g208,g170)
    c: Vertical(g204)
    c: Vertical(g208)
    c: Horizontal(g205)
    c: Horizontal(g207)
    c: Coincident(g165,g209)
    c: Coincident(g209,g210)
    c: Horizontal(g210)
    c: Coincident(g210,g211)
    c: Vertical(g211)
    c: Coincident(g211,g212)
    c: Horizontal(g212)
    c: Coincident(g212,g213)
    c: Coincident(g213,g167)
    c: Vertical(g213)
    c: Vertical(g209)
    c: Equal(g174,g178)
    c: Equal(g178,g189)
    c: Equal(g189,g193)
    c: Equal(g193,g179)
    c: Equal(g179,g183)
    c: Equal(g183,g184)
    c: Equal(g184,g188)
    c: DistanceX(g174,g174) = 4.5
    c: Equal(g175,g182)
    c: Equal(g182,g187)
    c: Equal(g187,g190)
    c: DistanceY(g175,g175) = 2
    c: Equal(g194,g198)
    c: Equal(g198,g199)
    c: Equal(g199,g203)
    c: Equal(g203,g213)
    c: Equal(g213,g209)
    c: Equal(g209,g204)
    c: Equal(g204,g208)
    c: Equal(g195,g200)
    c: Equal(g200,g207)
    c: Equal(g207,g212)
    c: DistanceY(g194,g194) = 4.5
    c: DistanceX(g195,g195) = 2
FEATURE [PartDesign::Pad] Pad
  AllowMultiFace = false
  Direction = (0,0,1)
  Length = 10
  Length2 = 100
  Profile = -> Sketch
  Type = 0
FEATURE [PartDesign::Body] Body
  Group = -> [Sketch,Pad]
  Origin = -> Origin
  Tip = -> Pad
FEATURE [TechDraw::DrawSVGTemplate] Template
  EditableTexts = AUTHOR_NAME=Sövény Gergely; DN=DN; DRAWING_TITLE=Cardboard Insert; FC-DATE=DD/MM/YYYY; FC-REV=REV A; FC-SC=SCALE; FC-SH=X / Y; FC-SI=A2; FreeCAD_DRAWING=FreeCAD DRAWING; PN=PN; SI-1=2020.11.13.
  Height = 420
  Orientation = 1
  Width = 594
FEATURE [TechDraw::DrawProjGroupItem] ProjItem  label="Front"
  CoarseView = false
  Direction = (0,0,1)
  Focus = 100
  HardHidden = false
  IsoCount = 0
  IsoHidden = false
  IsoVisible = false
  LockPosition = true
  Perspective = false
  Rotation = 0
  RotationVector = (1,0,0)
  ScaleType = 2
  SeamHidden = false
  SeamVisible = false
  SmoothHidden = false
  SmoothVisible = false
  Source = -> [Pad]
  Type = 0
  X = 0
  XDirection = (1,0,0)
  Y = 0
FEATURE [TechDraw::DrawProjGroup] ProjGroup
  Anchor = -> ProjItem
  AutoDistribute = true
  LockPosition = false
  ProjectionType = 0
  Rotation = 0
  ScaleType = 0
  Source = -> [Pad]
  Views = -> [ProjItem]
  X = 212.007
  Y = 217.711
  spacingX = 15
  spacingY = 15
FEATURE [TechDraw::DrawViewDimension] Dimension
  AngleOverride = false
  Arbitrary = false
  ArbitraryTolerances = false
  EqualTolerance = false
  ExtensionAngle = 0
  FormatSpec = %.2f
  FormatSpecOverTolerance = %+.2f
  FormatSpecUnderTolerance = %+.2f
  Inverted = false
  LineAngle = 0
  LockPosition = false
  MeasureType = 1
  OverTolerance = 0
  References2D = -> [ProjItem]
  Rotation = 0
  ScaleType = 0
  TheoreticalExact = false
  Type = 1
  UnderTolerance = 0
  X = -6.47208
  Y = 152.653
FEATURE [TechDraw::DrawPage] Page
  KeepUpdated = true
  NextBalloonIndex = 1
  ProjectionType = 0
  Template = -> Template
  Views = -> [ProjGroup,Dimension]
FEATURE [Sketcher::SketchObject] Sketch001
  FullyConstrained = true
  MapMode = 5
  Support = -> [XY_Plane001]
  sketch-geometry (80):
    g0: LineSegment StartX=-30 StartY=31 StartZ=0 EndX=30 EndY=31 EndZ=0
    g1: LineSegment StartX=30 StartY=31 StartZ=0 EndX=30 EndY=-31 EndZ=0
    g2: LineSegment StartX=30 StartY=-31 StartZ=0 EndX=-30 EndY=-31 EndZ=0
    g3: LineSegment StartX=-30 StartY=-31 StartZ=0 EndX=-30 EndY=31 EndZ=0
    g4: LineSegment StartX=-30 StartY=31 StartZ=0 EndX=-3.6e-15 EndY=0 EndZ=0
    g5: LineSegment StartX=-3.6e-15 StartY=0 StartZ=0 EndX=30 EndY=31 EndZ=0
    g6: LineSegment StartX=-30 StartY=-31 StartZ=0 EndX=-3.6e-15 EndY=0 EndZ=0
    g7: LineSegment StartX=-30 StartY=31 StartZ=0 EndX=-30 EndY=44 EndZ=0
    g8: LineSegment StartX=30 StartY=44 StartZ=0 EndX=30 EndY=31 EndZ=0
    g9: LineSegment StartX=-30 StartY=44 StartZ=0 EndX=-10 EndY=44 EndZ=0
    g10: LineSegment StartX=-10 StartY=44 StartZ=0 EndX=10 EndY=44 EndZ=0
    g11: LineSegment StartX=10 StartY=44 StartZ=0 EndX=30 EndY=44 EndZ=0
    g12: LineSegment StartX=-10 StartY=44 StartZ=0 EndX=-10 EndY=31 EndZ=0
    g13: LineSegment StartX=-10 StartY=31 StartZ=0 EndX=10 EndY=31 EndZ=0
    g14: LineSegment StartX=10 StartY=31 StartZ=0 EndX=10 EndY=44 EndZ=0
    g15: LineSegment StartX=10 StartY=44 StartZ=0 EndX=10 EndY=60 EndZ=0
    g16: LineSegment StartX=6 StartY=64 StartZ=0 EndX=-6 EndY=64 EndZ=0
    g17: LineSegment StartX=-10 StartY=60 StartZ=0 EndX=-10 EndY=44 EndZ=0
    g18: ArcOfCircle CenterX=-6 CenterY=60 CenterZ=0 NormalX=0 NormalY=0 NormalZ=1 AngleXU=0 Radius=4 StartAngle=1.5708 EndAngle=3.14159
    g19: ArcOfCircle CenterX=6 CenterY=60 CenterZ=0 NormalX=0 NormalY=0 NormalZ=1 AngleXU=0 Radius=4 StartAngle=7e-16 EndAngle=1.5708
    g20: LineSegment StartX=-30 StartY=31 StartZ=0 EndX=-43 EndY=31 EndZ=0
    g21: LineSegment StartX=-43 StartY=31 StartZ=0 EndX=-43 EndY=-31 EndZ=0
    g22: LineSegment StartX=-43 StartY=-31 StartZ=0 EndX=-30 EndY=-31 EndZ=0
    g23: LineSegment StartX=30 StartY=31 StartZ=0 EndX=43 EndY=31 EndZ=0
    g24: LineSegment StartX=43 StartY=31 StartZ=0 EndX=43 EndY=-31 EndZ=0
    g25: LineSegment StartX=43 StartY=-31 StartZ=0 EndX=30 EndY=-31 EndZ=0
    g26: LineSegment StartX=30 StartY=-31 StartZ=0 EndX=30 EndY=-44 EndZ=0
    g27: LineSegment StartX=30 StartY=-44 StartZ=0 EndX=-30 EndY=-44 EndZ=0
    g28: LineSegment StartX=-30 StartY=-44 StartZ=0 EndX=-30 EndY=-31 EndZ=0
    g29: LineSegment StartX=30 StartY=44 StartZ=0 EndX=60 EndY=77.5 EndZ=0
    g30: LineSegment StartX=60 StartY=77.5 StartZ=0 EndX=-60 EndY=77.5 EndZ=0
    g31: LineSegment StartX=-60 StartY=77.5 StartZ=0 EndX=-30 EndY=44 EndZ=0
    g32: LineSegment StartX=-43 StartY=31 StartZ=0 EndX=-73 EndY=64.5 EndZ=0
    g33: LineSegment StartX=-73 StartY=64.5 StartZ=0 EndX=-73 EndY=-64.5 EndZ=0
    g34: LineSegment StartX=-73 StartY=-64.5 StartZ=0 EndX=-43 EndY=-31 EndZ=0
    g35: LineSegment StartX=-30 StartY=-44 StartZ=0 EndX=-60 EndY=-77.5 EndZ=0
    g36: LineSegment StartX=-60 StartY=-77.5 StartZ=0 EndX=60 EndY=-77.5 EndZ=0
    g37: LineSegment StartX=60 StartY=-77.5 StartZ=0 EndX=30 EndY=-44 EndZ=0
    g38: LineSegment StartX=43 StartY=-31 StartZ=0 EndX=73 EndY=-64.5 EndZ=0
    g39: LineSegment StartX=73 StartY=-64.5 StartZ=0 EndX=73 EndY=64.5 EndZ=0
    g40: LineSegment StartX=73 StartY=64.5 StartZ=0 EndX=43 EndY=31 EndZ=0
    g41: Circle CenterX=-20 CenterY=-37 CenterZ=0 NormalX=0 NormalY=0 NormalZ=1 AngleXU=0 Radius=3
    g42: LineSegment StartX=-20 StartY=-37 StartZ=0 EndX=-20 EndY=-31 EndZ=0
    g43: LineSegment StartX=-60 StartY=115.5 StartZ=0 EndX=60 EndY=115.5 EndZ=0
    g44: LineSegment StartX=60 StartY=115.5 StartZ=0 EndX=60 EndY=77.5 EndZ=0
    g45: LineSegment StartX=-60 StartY=77.5 StartZ=0 EndX=-60 EndY=115.5 EndZ=0
    g46: LineSegment StartX=73 StartY=64.5 StartZ=0 EndX=111 EndY=64.5 EndZ=0
    g47: LineSegment StartX=111 StartY=64.5 StartZ=0 EndX=111 EndY=-64.5 EndZ=0
    g48: LineSegment StartX=111 StartY=-64.5 StartZ=0 EndX=73 EndY=-64.5 EndZ=0
    g49: LineSegment StartX=-60 StartY=-115.5 StartZ=0 EndX=60 EndY=-115.5 EndZ=0
    g50: LineSegment StartX=60 StartY=-115.5 StartZ=0 EndX=60 EndY=-77.5 EndZ=0
    g51: LineSegment StartX=-60 StartY=-77.5 StartZ=0 EndX=-60 EndY=-115.5 EndZ=0
    g52: LineSegment StartX=-111 StartY=64.5 StartZ=0 EndX=-73 EndY=64.5 EndZ=0
    g53: LineSegment StartX=-73 StartY=-64.5 StartZ=0 EndX=-111 EndY=-64.5 EndZ=0
    g54: LineSegment StartX=-111 StartY=-64.5 StartZ=0 EndX=-111 EndY=64.5 EndZ=0
    g55: LineSegment StartX=-30 StartY=10 StartZ=0 EndX=-30 EndY=-10 EndZ=0
    g56: LineSegment StartX=-30 StartY=-10 StartZ=0 EndX=-5 EndY=-2.5 EndZ=0
    g57: LineSegment StartX=-5 StartY=-2.5 StartZ=0 EndX=-5 EndY=2.5 EndZ=0
    g58: LineSegment StartX=-5 StartY=2.5 StartZ=0 EndX=-30 EndY=10 EndZ=0
    g59: LineSegment StartX=30 StartY=10 StartZ=0 EndX=5 EndY=2.5 EndZ=0
    g60: LineSegment StartX=5 StartY=2.5 StartZ=0 EndX=5 EndY=-2.5 EndZ=0
    g61: LineSegment StartX=5 StartY=-2.5 StartZ=0 EndX=30 EndY=-10 EndZ=0
    g62: LineSegment StartX=30 StartY=-10 StartZ=0 EndX=30 EndY=-20 EndZ=0
    g63: LineSegment StartX=30 StartY=-20 StartZ=0 EndX=-30 EndY=-20 EndZ=0
    g64: LineSegment StartX=-30 StartY=-20 StartZ=0 EndX=-30 EndY=-10 EndZ=0
    g65: LineSegment StartX=-30 StartY=10 StartZ=0 EndX=-30 EndY=20 EndZ=0
    g66: LineSegment StartX=-30 StartY=20 StartZ=0 EndX=30 EndY=20 EndZ=0
    g67: LineSegment StartX=30 StartY=20 StartZ=0 EndX=30 EndY=10 EndZ=0
    g68: LineSegment StartX=-5 StartY=2.5 StartZ=0 EndX=5 EndY=2.5 EndZ=0
    g69: LineSegment StartX=-5 StartY=2.5 StartZ=0 EndX=-3.6e-15 EndY=0 EndZ=0
    g70: LineSegment StartX=-3.6e-15 StartY=0 StartZ=0 EndX=-5 EndY=-2.5 EndZ=0
    g71: LineSegment StartX=-3.6e-15 StartY=0 StartZ=0 EndX=5 EndY=2.5 EndZ=0
    g72: LineSegment StartX=-5 StartY=2.5 StartZ=0 EndX=-2 EndY=12.5 EndZ=0
    g73: LineSegment StartX=-2 StartY=12.5 StartZ=0 EndX=-30 EndY=10 EndZ=0
    g74: LineSegment StartX=5 StartY=2.5 StartZ=0 EndX=2 EndY=12.5 EndZ=0
    g75: LineSegment StartX=2 StartY=12.5 StartZ=0 EndX=30 EndY=10 EndZ=0
    g76: LineSegment StartX=30 StartY=-10 StartZ=0 EndX=2 EndY=-12.5 EndZ=0
    g77: LineSegment StartX=2 StartY=-12.5 StartZ=0 EndX=5 EndY=-2.5 EndZ=0
    g78: LineSegment StartX=-5 StartY=-2.5 StartZ=0 EndX=-2 EndY=-12.5 EndZ=0
    g79: LineSegment StartX=-2 StartY=-12.5 StartZ=0 EndX=-30 EndY=-10 EndZ=0
  constraints (212):
    c: Coincident(g0,g1)
    c: Coincident(g1,g2)
    c: Coincident(g2,g3)
    c: Coincident(g3,g0)
    c: Horizontal(g0)
    c: Horizontal(g2)
    c: Vertical(g1)
    c: Vertical(g3)
    c: Coincident(g0,g4)
    c: Coincident(g4,g-1)
    c: Coincident(g4,g5)
    c: Coincident(g5,g0)
    c: Coincident(g6,g4)
    c: Coincident(g6,g2)
    c: Equal(g6,g4)
    c: Equal(g4,g5)
    c: DistanceX(g0,g0) = 60
    c: DistanceY(g3,g3) = 62
    c: Coincident(g0,g7)
    c: Vertical(g7)
    c: Coincident(g7,g9)
    c: Coincident(g11,g8)
    c: Coincident(g8,g0)
    c: Vertical(g8)
    c: DistanceY(g7,g7) = 13
    c: Coincident(g9,g10)
    c: Horizontal(g9)
    c: Coincident(g10,g11)
    c: Horizontal(g10)
    c: Horizontal(g11)
    c: Coincident(g9,g12)
    c: Vertical(g12)
    c: Coincident(g12,g13)
    c: Horizontal(g13)
    c: Coincident(g13,g14)
    c: Coincident(g14,g11)
    c: Vertical(g14)
    c: Equal(g9,g11)
    c: PointOnObject(g13,g0)
    c: Horizontal(g16)
    c: Vertical(g15)
    c: Vertical(g17)
    c: Coincident(g15,g11)
    c: Coincident(g17,g9)
    c: Tangent(g16,g18) = -1.5708
    c: Tangent(g17,g18) = -1.5708
    c: Tangent(g15,g19) = -1.5708
    c: Tangent(g16,g19) = -1.5708
    c: Equal(g19,g18)
    c: DistanceX(g13,g13) = 20
    c: DistanceY(g9,g16) = 20
    c: Coincident(g20,g21)
    c: Coincident(g21,g22)
    c: Horizontal(g20)
    c: Horizontal(g22)
    c: Vertical(g21)
    c: Coincident(g20,g7)
    c: Coincident(g22,g2)
    c: Coincident(g23,g24)
    c: Coincident(g24,g25)
    c: Horizontal(g23)
    c: Horizontal(g25)
    c: Vertical(g24)
    c: Coincident(g23,g8)
    c: Coincident(g25,g1)
    c: Coincident(g26,g27)
    c: Coincident(g27,g28)
    c: Horizontal(g27)
    c: Vertical(g26)
    c: Vertical(g28)
    c: Coincident(g26,g25)
    c: Equal(g26,g25)
    c: Equal(g25,g20)
    c: Equal(g20,g7)
    c: Coincident(g28,g22)
    c: Coincident(g8,g29)
    c: Coincident(g29,g30)
    c: Horizontal(g30)
    c: Coincident(g30,g31)
    c: Coincident(g31,g7)
    c: Coincident(g20,g32)
    c: Coincident(g32,g33)
    c: Vertical(g33)
    c: Coincident(g33,g34)
    c: Coincident(g34,g22)
    c: Coincident(g28,g35)
    c: Coincident(g35,g36)
    c: Horizontal(g36)
    c: Coincident(g36,g37)
    c: Coincident(g37,g26)
    c: Coincident(g25,g38)
    c: Coincident(g38,g39)
    c: Vertical(g39)
    c: Coincident(g39,g40)
    c: Coincident(g40,g23)
    c: Equal(g32,g31)
    c: Equal(g31,g29)
    c: Equal(g29,g40)
    c: Equal(g40,g38)
    c: Equal(g38,g37)
    c: Equal(g37,g35)
    c: Equal(g35,g34)
    c: Parallel(g32,g31)
    c: Parallel(g31,g37)
    c: Parallel(g37,g38)
    c: DistanceX(g32,g32) = 30
    c: DistanceY(g7,g30) = 33.5
    c: Radius(g19) = 4
    c: Diameter(g41) = 6
    c: Coincident(g42,g41)
    c: PointOnObject(g42,g2)
    c: Vertical(g42)
    c: DistanceY(g42,g42) = 6
    c: DistanceX(g42,g4) = 20
    c: Coincident(g43,g44)
    c: Coincident(g45,g43)
    c: Horizontal(g43)
    c: Vertical(g44)
    c: Vertical(g45)
    c: Coincident(g44,g29)
    c: Coincident(g31,g45)
    c: Coincident(g46,g47)
    c: Coincident(g47,g48)
    c: Horizontal(g46)
    c: Horizontal(g48)
    c: Vertical(g47)
    c: Coincident(g48,g38)
    c: Coincident(g40,g46)
    c: Coincident(g49,g50)
    c: Coincident(g51,g49)
    c: Horizontal(g49)
    c: Vertical(g50)
    c: Vertical(g51)
    c: Coincident(g50,g37)
    c: Coincident(g51,g35)
    c: Coincident(g53,g54)
    c: Coincident(g54,g52)
    c: Horizontal(g52)
    c: Horizontal(g53)
    c: Vertical(g54)
    c: Coincident(g52,g32)
    c: Coincident(g53,g34)
    c: Equal(g53,g51)
    c: Equal(g51,g48)
    c: Equal(g48,g45)
    c: DistanceX(g52,g52) = 38
    c: Vertical(g55)
    c: Coincident(g55,g56)
    c: Coincident(g56,g57)
    c: Vertical(g57)
    c: Coincident(g57,g58)
    c: Coincident(g58,g55)
    c: DistanceX(g58,g58) = 25
    c: Coincident(g59,g60)
    c: Vertical(g60)
    c: Coincident(g60,g61)
    c: Coincident(g61,g62)
    c: Vertical(g62)
    c: Coincident(g62,g63)
    c: Horizontal(g63)
    c: Coincident(g63,g64)
    c: Coincident(g64,g55)
    c: Vertical(g64)
    c: Coincident(g58,g65)
    c: Vertical(g65)
    c: Coincident(g65,g66)
    c: Horizontal(g66)
    c: Coincident(g66,g67)
    c: Coincident(g67,g59)
    c: Vertical(g67)
    c: Equal(g57,g60)
    c: Coincident(g57,g68)
    c: Coincident(g68,g59)
    c: Horizontal(g68)
    c: Coincident(g57,g69)
    c: Coincident(g69,g4)
    c: Coincident(g69,g70)
    c: Coincident(g70,g56)
    c: Coincident(g4,g71)
    c: Coincident(g71,g59)
    c: Equal(g71,g69)
    c: Equal(g69,g70)
    c: DistanceY(g57,g57) = 5
    c: DistanceY(g55,g55) = 20
    c: Equal(g65,g64)
    c: Equal(g64,g62)
    c: Equal(g62,g67)
    c: Equal(g61,g56)
    c: Equal(g56,g58)
    c: Equal(g58,g59)
    c: DistanceX(g63,g63) = 60
    c: Coincident(g57,g72)
    c: Coincident(g72,g73)
    c: Coincident(g73,g65)
    c: Perpendicular(g58,g72)
    c: DistanceY(g72,g72) = 10
    c: Coincident(g60,g74)
    c: Coincident(g74,g75)
    c: Coincident(g75,g67)
    c: Coincident(g62,g76)
    c: Coincident(g76,g77)
    c: Coincident(g77,g60)
    c: Coincident(g57,g78)
    c: Coincident(g78,g79)
    c: Coincident(g79,g64)
    c: Equal(g78,g72)
    c: Equal(g72,g74)
    c: Equal(g74,g77)
    c: Equal(g79,g76)
    c: Equal(g76,g75)
    c: Equal(g75,g73)
    c: DistanceY(g65,g65) = 10
FEATURE [PartDesign::Pad] Pad001
  Direction = (0,0,1)
  Length = 1
  Length2 = 10
  Profile = -> Sketch001
  ReferenceAxis = -> Sketch001 [N_Axis]
  Type = 0
FEATURE [PartDesign::Body] Body001
  Group = -> [Sketch001,Pad001]
  Origin = -> Origin001
  Tip = -> Pad001
FEATURE [TechDraw::DrawSVGTemplate] Template001
  EditableTexts = Designed_by_Name=Designed by Name; Drawing_number=Drawing number; FC-Date=Date; FC-SC=Scale; FC-SH=Sheet; FC-Title=Title; Subtitle=Subtitle; Weight=Weight
  Height = 210
  Orientation = 1
  Width = 297
FEATURE [TechDraw::DrawProjGroupItem] ProjItem001  label="Front001"
  CoarseView = false
  Direction = (0,0,1)
  Focus = 100
  HardHidden = false
  IsoCount = 0
  IsoHidden = false
  IsoVisible = false
  LockPosition = true
  Perspective = false
  Rotation = 0
  RotationVector = (-1,0,0)
  ScaleType = 2
  SeamHidden = false
  SeamVisible = true
  SmoothHidden = false
  SmoothVisible = true
  Source = -> [Pad001]
  Type = 0
  X = 0
  XDirection = (-1,0,0)
  Y = 0
FEATURE [TechDraw::DrawProjGroup] ProjGroup001
  Anchor = -> ProjItem001
  AutoDistribute = true
  LockPosition = false
  ProjectionType = 0
  Rotation = 0
  ScaleType = 0
  Source = -> [Pad001]
  Views = -> [ProjItem001]
  X = 135.994
  Y = 108.461
  spacingX = 15
  spacingY = 15
FEATURE [TechDraw::DrawViewDimension] Dimension001
  AngleOverride = false
  Arbitrary = false
  ArbitraryTolerances = false
  EqualTolerance = true
  ExtensionAngle = 0
  FormatSpec = %.2w
  FormatSpecOverTolerance = %+.2w
  FormatSpecUnderTolerance = %+.2w
  Inverted = false
  LineAngle = 0
  LockPosition = false
  MeasureType = 1
  OverTolerance = 0
  References2D = -> [ProjItem001]
  Rotation = 0
  ScaleType = 0
  TheoreticalExact = false
  Type = 1
  UnderTolerance = 0
  X = -0.896697
  Y = 89.544
FEATURE [TechDraw::DrawPage] Page001
  KeepUpdated = true
  NextBalloonIndex = 1
  ProjectionType = 0
  Template = -> Template001
  Views = -> [ProjGroup001,Dimension001]
